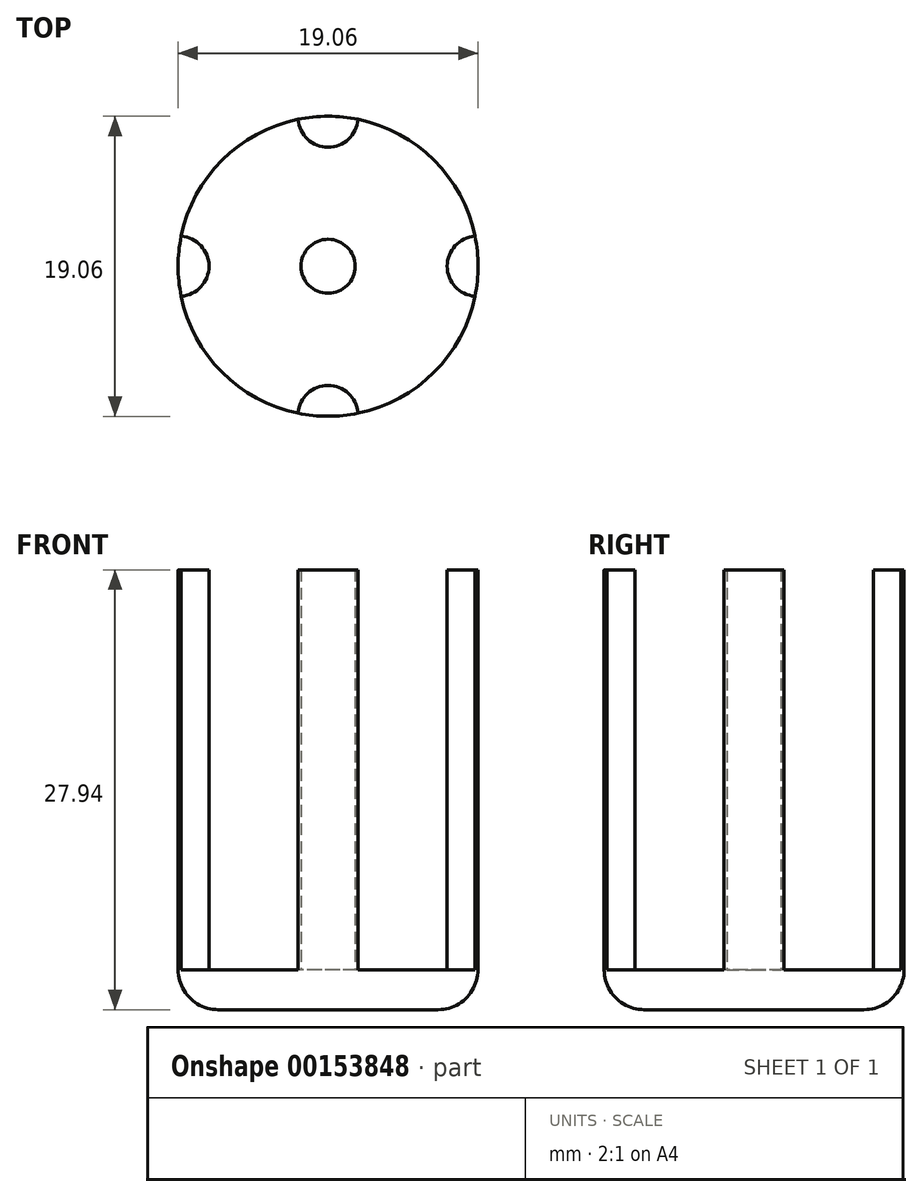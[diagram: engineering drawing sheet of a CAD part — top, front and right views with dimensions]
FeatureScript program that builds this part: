
annotation { "Feature Type Name" : "Feature", "Feature Type Description" : "" }
export const myFeature = defineFeature(function(context is Context, id is Id, definition is map)
    precondition{}
    {
        {
            var Q0;
            Q0=qCreatedBy(makeId("Top.planeOp"),FACE);
            var sketch = newSketch(context, id + "F0", { "sketchPlane" : qUnion([Q0])});
            skCircle(sketch, "E0", {"center": v(0, 0) * mm, "radius": 9.53 * mm});
            skSolve(sketch);
        }
        {
            var Q0;
            Q0=makeQuery(id+"F0.imprint","IMPRINT",FACE,{"disambiguationData":[TD([[makeQuery(id+"F0.imprint","IMPRINT",EDGE,{"derivedFrom":sQuery(id+"F0.wireOp",EDGE,"E0")}),1.0]])]});
            extrude(context, id + "F1", {"entities" : qUnion([Q0]), "depth" : 2.54 * mm});
        }
        {
            var Q0;
            Q0=makeQuery(id+"F1.opExtrude","CAP_FACE",FACE,{"disambiguationData":[OSD([sQuery(id+"F0.wireOp",EDGE,"E0")])],"isStart":false});
            var sketch = newSketch(context, id + "F2", { "sketchPlane" : qUnion([Q0])});
            skCircle(sketch, "E1", {"center": v(0, 0) * mm, "radius": 1.71 * mm});
            skArc(sketch, "E2", {"start": v(9.33, 1.9) * mm, "mid": v(7.56, 0) * mm, "end": v(9.33, -1.9) * mm});
            skArc(sketch, "E3.1.0", {"start": v(-1.9, 9.33) * mm, "mid": v(0, 7.56) * mm, "end": v(1.9, 9.33) * mm});
            skArc(sketch, "E3.2.0", {"start": v(-9.33, -1.9) * mm, "mid": v(-7.56, 0) * mm, "end": v(-9.33, 1.9) * mm});
            skArc(sketch, "E3.3.0", {"start": v(1.9, -9.33) * mm, "mid": v(0, -7.56) * mm, "end": v(-1.9, -9.33) * mm});
            skCircle(sketch, "E4", {"center": v(0, 0) * mm, "radius": 9.52 * mm});
            skSolve(sketch);
        }
        {
            var Q0;
            {var subQ0=sQuery(id+"F2.wireOp",EDGE,"E2");Q0=makeQuery(id+"F2.imprint","IMPRINT",FACE,{"disambiguationData":[TD([[makeQuery(id+"F2.imprint","IMPRINT",EDGE,{"derivedFrom":subQ0}),1.0]])]});}
            var Q1;
            {var subQ0=sQuery(id+"F2.wireOp",EDGE,"E3.1.0");Q1=makeQuery(id+"F2.imprint","IMPRINT",FACE,{"disambiguationData":[TD([[makeQuery(id+"F2.imprint","IMPRINT",EDGE,{"derivedFrom":subQ0}),1.0]])]});}
            var Q2;
            {var subQ0=sQuery(id+"F2.wireOp",EDGE,"E3.2.0");Q2=makeQuery(id+"F2.imprint","IMPRINT",FACE,{"disambiguationData":[TD([[makeQuery(id+"F2.imprint","IMPRINT",EDGE,{"derivedFrom":subQ0}),1.0]])]});}
            var Q3;
            {var subQ0=sQuery(id+"F2.wireOp",EDGE,"E3.3.0");Q3=makeQuery(id+"F2.imprint","IMPRINT",FACE,{"disambiguationData":[TD([[makeQuery(id+"F2.imprint","IMPRINT",EDGE,{"derivedFrom":subQ0}),1.0]])]});}
            var Q4;
            Q4=makeQuery(id+"F2.imprint","IMPRINT",FACE,{"disambiguationData":[TD([[makeQuery(id+"F2.imprint","IMPRINT",EDGE,{"derivedFrom":sQuery(id+"F2.wireOp",EDGE,"E1")}),1.0]])]});
            extrude(context, id + "F3", {"entities" : qUnion([Q0, Q1, Q2, Q3, Q4]), "operationType" : NewBodyOperationType.ADD, "depth" : 25.4 * mm});
        }
        {
            var Q0;
            Q0=makeQuery(id+"F1.opExtrude","CAP_EDGE",EDGE,{"disambiguationData":[OSD([sQuery(id+"F0.wireOp",EDGE,"E0")])],"isStart":true});
            fillet(context, id + "F4", {"entities" : qUnion([Q0]), "radius" : 2.54 * mm, "tangentPropagation" : true, "allowEdgeOverflow" : false});
        }
    });
